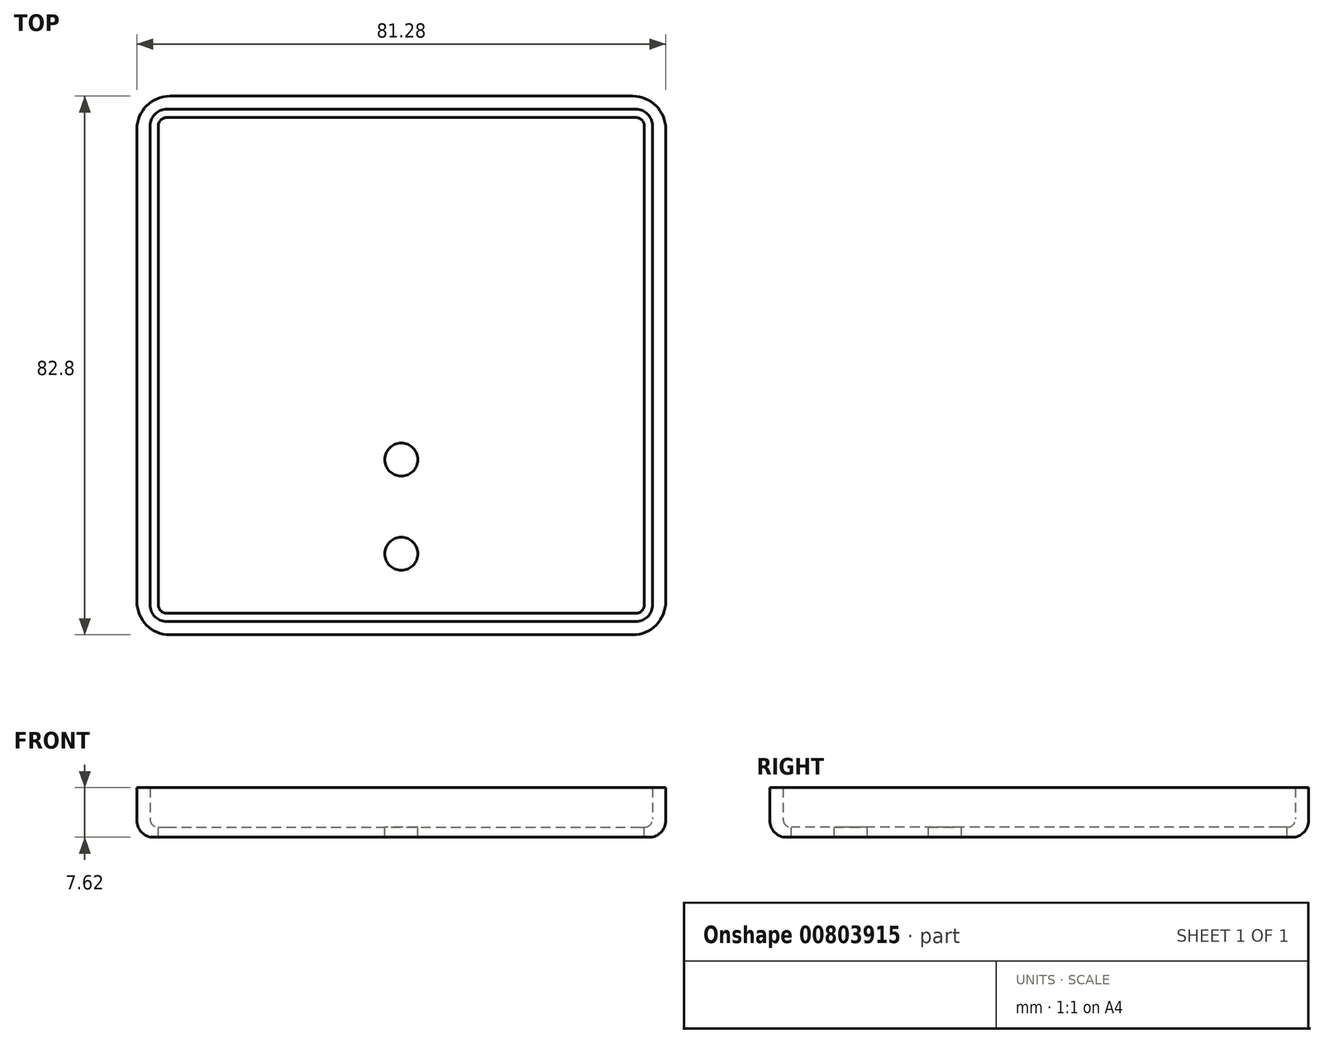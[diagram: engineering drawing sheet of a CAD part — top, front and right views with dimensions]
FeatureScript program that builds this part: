
annotation { "Feature Type Name" : "Feature", "Feature Type Description" : "" }
export const myFeature = defineFeature(function(context is Context, id is Id, definition is map)
    precondition{}
    {
        {
            var Q0;
            Q0=qCreatedBy(makeId("Top.planeOp"),FACE);
            var sketch = newSketch(context, id + "F0", { "sketchPlane" : qUnion([Q0])});
            skLineSegment(sketch, "E0.bottom", {"start": v(-40.64, 41.4) * mm, "end": v(40.64, 41.4) * mm});
            skLineSegment(sketch, "E0.top", {"start": v(-40.64, -41.4) * mm, "end": v(40.64, -41.4) * mm});
            skLineSegment(sketch, "E0.left", {"start": v(-40.64, 41.4) * mm, "end": v(-40.64, -41.4) * mm});
            skLineSegment(sketch, "E0.right", {"start": v(40.64, 41.4) * mm, "end": v(40.64, -41.4) * mm});
            skPoint(sketch, "E0.middle", {"position": v(0, 0) * mm});
            skLineSegment(sketch, "E1.bottom", {"start": v(-38.6, 39.37) * mm, "end": v(38.6, 39.37) * mm});
            skLineSegment(sketch, "E1.top", {"start": v(-38.6, -39.37) * mm, "end": v(38.6, -39.37) * mm});
            skLineSegment(sketch, "E1.left", {"start": v(-38.6, 39.37) * mm, "end": v(-38.6, -39.37) * mm});
            skLineSegment(sketch, "E1.right", {"start": v(38.6, 39.37) * mm, "end": v(38.6, -39.37) * mm});
            skSolve(sketch);
        }
        {
            var Q0;
            Q0=makeQuery(id+"F0.imprint","IMPRINT",FACE,{"disambiguationData":[TD([[makeQuery(id+"F0.imprint","IMPRINT",EDGE,{"derivedFrom":sQuery(id+"F0.wireOp",EDGE,"E0.bottom")}),1.0]])]});
            var Q1;
            Q1=makeQuery(id+"F0.imprint","IMPRINT",FACE,{"disambiguationData":[TD([[makeQuery(id+"F0.imprint","IMPRINT",EDGE,{"derivedFrom":sQuery(id+"F0.wireOp",EDGE,"E0.bottom")}),-1.0]])]});
            extrude(context, id + "F1", {"entities" : qUnion([Q0, Q1]), "depth" : 7.62 * mm, "offsetDistance" : 25.4 * mm});
        }
        {
            var Q0;
            Q0=makeQuery(id+"F0.imprint","IMPRINT",FACE,{"disambiguationData":[TD([[makeQuery(id+"F0.imprint","IMPRINT",EDGE,{"derivedFrom":sQuery(id+"F0.wireOp",EDGE,"E0.bottom")}),-1.0]])]});
            var Q1;
            Q1=makeQuery(id+"F0.imprint","IMPRINT",FACE,{"disambiguationData":[TD([[makeQuery(id+"F0.imprint","IMPRINT",EDGE,{"derivedFrom":sQuery(id+"F0.wireOp",EDGE,"E1.bottom")}),-1.0]])]});
            extrude(context, id + "F2", {"entities" : qUnion([Q0, Q1]), "operationType" : NewBodyOperationType.ADD, "depth" : 1.52 * mm, "offsetDistance" : 25.4 * mm});
        }
        {
            var Q0;
            Q0=makeQuery(id+"F1.opExtrude","SWEPT_EDGE",EDGE,{"disambiguationData":[OSD([sQuery(id+"F0.wireOp",EDGE,"E1.bottom"),sQuery(id+"F0.wireOp",EDGE,"E1.left")])]});
            var Q1;
            Q1=makeQuery(id+"F1.opExtrude","SWEPT_EDGE",EDGE,{"disambiguationData":[OSD([sQuery(id+"F0.wireOp",EDGE,"E1.bottom"),sQuery(id+"F0.wireOp",EDGE,"E1.right")])]});
            var Q2;
            Q2=makeQuery(id+"F1.opExtrude","SWEPT_EDGE",EDGE,{"disambiguationData":[OSD([sQuery(id+"F0.wireOp",EDGE,"E1.top"),sQuery(id+"F0.wireOp",EDGE,"E1.right")])]});
            var Q3;
            Q3=makeQuery(id+"F1.opExtrude","SWEPT_EDGE",EDGE,{"disambiguationData":[OSD([sQuery(id+"F0.wireOp",EDGE,"E1.top"),sQuery(id+"F0.wireOp",EDGE,"E1.left")])]});
            var Q4;
            {var subQ0=sQuery(id+"F0.wireOp",EDGE,"E0.right");var subQ1=sQuery(id+"F0.wireOp",EDGE,"E0.left");var subQ2=sQuery(id+"F0.wireOp",EDGE,"E0.top");var subQ3=sQuery(id+"F0.wireOp",EDGE,"E0.bottom");Q4=makeQuery(id+"F2.boolean.opBoolean","MERGE",FACE,{"derivedFrom":[makeQuery(id+"F1.opExtrude","CAP_FACE",FACE,{"disambiguationData":[OSD([subQ3,subQ2,subQ1,subQ0,sQuery(id+"F0.wireOp",EDGE,"E1.bottom"),sQuery(id+"F0.wireOp",EDGE,"E1.top"),sQuery(id+"F0.wireOp",EDGE,"E1.left"),sQuery(id+"F0.wireOp",EDGE,"E1.right")])],"isStart":true}),makeQuery(id+"F2.opExtrude","CAP_FACE",FACE,{"disambiguationData":[OSD([subQ3,subQ2,subQ1,subQ0])],"isStart":true})]});}
            fillet(context, id + "F3", {"entities" : qUnion([Q0, Q1, Q2, Q3, Q4]), "radius" : 2.54 * mm, "tangentPropagation" : true, "allowEdgeOverflow" : false});
        }
        {
            var Q0;
            Q0=makeQuery(id+"F2.opExtrude","CAP_FACE",FACE,{"disambiguationData":[OSD([sQuery(id+"F0.wireOp",EDGE,"E0.bottom"),sQuery(id+"F0.wireOp",EDGE,"E0.top"),sQuery(id+"F0.wireOp",EDGE,"E0.left"),sQuery(id+"F0.wireOp",EDGE,"E0.right")])],"isStart":false});
            fillet(context, id + "F4", {"entities" : qUnion([Q0]), "radius" : 1.27 * mm, "tangentPropagation" : true, "allowEdgeOverflow" : false});
        }
        {
            var Q0;
            Q0=makeQuery(id+"F2.opExtrude","CAP_FACE",FACE,{"disambiguationData":[OSD([sQuery(id+"F0.wireOp",EDGE,"E0.bottom"),sQuery(id+"F0.wireOp",EDGE,"E0.top"),sQuery(id+"F0.wireOp",EDGE,"E0.left"),sQuery(id+"F0.wireOp",EDGE,"E0.right")])],"isStart":false});
            var sketch = newSketch(context, id + "F5", { "sketchPlane" : qUnion([Q0])});
            skCircle(sketch, "E2", {"center": v(0, 0) * mm, "radius": 2.54 * mm});
            skCircle(sketch, "E3.0.1.0", {"center": v(0, 14.48) * mm, "radius": 2.54 * mm});
            skCircle(sketch, "E3.0.2.0", {"center": v(0, 28.96) * mm, "radius": 2.54 * mm});
            skLineSegment(sketch, "E3.direction1", {"start": v(0, 0) * mm, "end": v(20.57, 0) * mm, "construction": true});
            skLineSegment(sketch, "E3.direction2", {"start": v(0, 0) * mm, "end": v(0, 14.48) * mm, "construction": true});
            skCircle(sketch, "E4.MirrorC", {"center": v(0, -14.48) * mm, "radius": 2.54 * mm});
            skCircle(sketch, "E5.MirrorC", {"center": v(0, -28.96) * mm, "radius": 2.54 * mm});
            skSolve(sketch);
        }
        {
            var Q0;
            Q0=makeQuery(id+"F5.imprint","IMPRINT",FACE,{"disambiguationData":[TD([[makeQuery(id+"F5.imprint","IMPRINT",EDGE,{"derivedFrom":sQuery(id+"F5.wireOp",EDGE,"E3.0.2.0")}),1.0]])]});
            var Q1;
            Q1=makeQuery(id+"F5.imprint","IMPRINT",FACE,{"disambiguationData":[TD([[makeQuery(id+"F5.imprint","IMPRINT",EDGE,{"derivedFrom":sQuery(id+"F5.wireOp",EDGE,"E3.0.1.0")}),1.0]])]});
            var Q2;
            Q2=makeQuery(id+"F5.imprint","IMPRINT",FACE,{"disambiguationData":[TD([[makeQuery(id+"F5.imprint","IMPRINT",EDGE,{"derivedFrom":sQuery(id+"F5.wireOp",EDGE,"E2")}),1.0]])]});
            var Q3;
            Q3=makeQuery(id+"F5.imprint","IMPRINT",FACE,{"disambiguationData":[TD([[makeQuery(id+"F5.imprint","IMPRINT",EDGE,{"derivedFrom":sQuery(id+"F5.wireOp",EDGE,"E4.MirrorC")}),-1.0]])]});
            var Q4;
            Q4=makeQuery(id+"F5.imprint","IMPRINT",FACE,{"disambiguationData":[TD([[makeQuery(id+"F5.imprint","IMPRINT",EDGE,{"derivedFrom":sQuery(id+"F5.wireOp",EDGE,"E5.MirrorC")}),-1.0]])]});
            extrude(context, id + "F6", {"entities" : qUnion([Q0, Q1, Q2, Q3, Q4]), "operationType" : NewBodyOperationType.REMOVE, "oppositeDirection" : true, "depth" : 25.4 * mm, "offsetDistance" : 25.4 * mm});
        }
        {
            var Q0;
            Q0=makeQuery(id+"F1.opExtrude","SWEPT_EDGE",EDGE,{"disambiguationData":[OSD([sQuery(id+"F0.wireOp",EDGE,"E0.top"),sQuery(id+"F0.wireOp",EDGE,"E0.right")])]});
            var Q1;
            Q1=makeQuery(id+"F1.opExtrude","SWEPT_EDGE",EDGE,{"disambiguationData":[OSD([sQuery(id+"F0.wireOp",EDGE,"E0.bottom"),sQuery(id+"F0.wireOp",EDGE,"E0.right")])]});
            var Q2;
            Q2=makeQuery(id+"F1.opExtrude","SWEPT_EDGE",EDGE,{"disambiguationData":[OSD([sQuery(id+"F0.wireOp",EDGE,"E0.bottom"),sQuery(id+"F0.wireOp",EDGE,"E0.left")])]});
            var Q3;
            Q3=makeQuery(id+"F1.opExtrude","SWEPT_EDGE",EDGE,{"disambiguationData":[OSD([sQuery(id+"F0.wireOp",EDGE,"E0.top"),sQuery(id+"F0.wireOp",EDGE,"E0.left")])]});
            fillet(context, id + "F7", {"entities" : qUnion([Q0, Q1, Q2, Q3]), "radius" : 5.08 * mm, "tangentPropagation" : true, "allowEdgeOverflow" : false});
        }
    });
